# Revit family: plfy-p22_71gmg7_60Hz
name_source: partatom
category: 機械設備
units: mm (PartAtom-declared; Revit-internal decimal feet)

## family parameters
OmniClass タイトル = Split System Air Conditioning Units
OmniClass 番号 = 23.75.10.24.21.27.27
パーツ タイプ = 標準
ロード時にボイドで切り取り = いいえ
丸型コネクタ寸法 = 直径を使用
作業面ベース = いいえ
共有 = いいえ
常に垂直 = はい
部屋計算ポイント = はい

## types (6) — shared parameters
Clearance Back = 500  [stored 1.64042 ft]
Clearance Bottom = 1000  [stored 3.28084 ft]
Clearance Front = 500  [stored 1.64042 ft]
Clearance Left = 500  [stored 1.64042 ft]
Clearance Right = 500  [stored 1.64042 ft]
Clearance Top = 305  [stored 1.00066 ft]
Depth = 670  [stored 2.19816 ft]
Height = 298  [stored 0.97769 ft]
IfcExportAs = IfcUnitaryEquipmentType
IfcExportType = AIRCONDITIONINGUNIT
OmniClassCode = 23-33 17 13 11
Panel Depth = 760  [stored 2.49344 ft]
Panel Height = 15  [stored 0.0492126 ft]
Panel Width = 760  [stored 2.49344 ft]
URL = https://www.mitsubishielectric.co.jp
Uniclass2015Code = Pr_70_65_03_84
Uniclass2015Title = Split coil remote air cooled condensing units
Uniclass2015Version = Systems v1.9
Width = 670  [stored 2.19816 ft]
ケーブルサイズ = 0 mm
サービススペース = はい
ドレン管径 = 25 mm
ドレン管径 (外径) = 32 mm
ドレン管高さ = 227  [stored 0.744751 ft]
パネルマテリアル = <カテゴリ別>
仕様書バージョン = Version1.0
企業コード = 108420
冷媒ガス管高さ = 183
冷媒液管高さ = 159  [stored 0.521654 ft]
冷媒管径 = 100 mm
冷媒高低圧ガス管径 = 0 mm
分類コード = 50053003123030
加湿給水管径 = 0 mm
参照している仕様書等のバージョン = 公共建築工事標準仕様書（機械設備工事編）平成31年度版
吊りボルト_H = 134
吊り位置X = 640  [stored 2.09974 ft]
吊り位置Y = 507  [stored 1.66339 ft]
周波数 = 60 Hz
呼称 = パッケージ形空気調和機_室内機
始動方式 = 直入
形式 = カセット形（4方向吹出形）
推奨ブレーカー容量 = 0 A
本体マテリアル = <カテゴリ別>
極数 = 1
法定耐用年数 = 6
消費電力_加湿器 = 0.00 kW
消費電力_電気ヒーター = 0.00 kW
発停方法 = 付属スイッチ
相 = 1
積算_科目 = 1 空気調和設備
符号 = PAC-CK4
製品リリース年月 = 2021/5/10
製品出荷対象 = 国内
製造元 = 三菱電機株式会社
設置方法 = カセット形
設計冷房能力 = 0 kW
設計冷房能力_顕熱 = 0 kW
設計暖房能力 = 0.00 kW
説明 = ビル用マルチ 4方向天井カセット形<コンパクトタイプ>
負荷分類 = 3_ファン類
運転質量 = 0.00 kg
電動機出力_送風機 = 0.05 kW
電圧 = 200 V
電圧_電気ヒーター = 0 V
zero-valued in all types: 価格, 有効加湿量, 電源_H

## per-type parameters (varying)
- 天井4方向_PLFY-P22GMG7: MAX風量=600.0 m³/h; MID風量=570.0 m³/h; MID風量2=540.0 m³/h; MIN風量=510.0 m³/h; 冷媒ガス管径=13 mm; 冷媒ガス管長さ=76  [stored 0.249344 ft]; 冷媒液管径=6 mm; 冷媒液管長さ=71  [stored 0.23294 ft]; 冷媒管径符号=Ac; 冷房能力=2.2 kW; 暖房能力=2.50 kW; 構成品番=PLFY-P22GMG; 消費電力=0.02 kW; 消費電力_冷房=0.02 kW; 消費電力_暖房=0.02 kW; 製品質量=19.60 kg; 質量=23.52 kg; 音響パワーレベル(dB)=50; 音響パワーレベル（中1）(dB)=49; 音響パワーレベル（中2）(dB)=48; 音響パワーレベル（弱）(dB)=47; 風量=600.0 m³/h; 風量（中）（m3／min）=9.5; 風量（弱）（m3／min）=9; 風量（強）（m3／min）=10; 風量（静）（m3／min）=8.5
- 天井4方向_PLFY-P28GMG7: MAX風量=600.0 m³/h; MID風量=570.0 m³/h; MID風量2=540.0 m³/h; MIN風量=510.0 m³/h; 冷媒ガス管径=13 mm; 冷媒ガス管長さ=76  [stored 0.249344 ft]; 冷媒液管径=6 mm; 冷媒液管長さ=71  [stored 0.23294 ft]; 冷媒管径符号=Ac; 冷房能力=2.8 kW; 暖房能力=3.20 kW; 構成品番=PLFY-P28GMG; 消費電力=0.02 kW; 消費電力_冷房=0.02 kW; 消費電力_暖房=0.02 kW; 製品質量=19.60 kg; 質量=23.52 kg; 音響パワーレベル(dB)=50; 音響パワーレベル（中1）(dB)=49; 音響パワーレベル（中2）(dB)=48; 音響パワーレベル（弱）(dB)=47; 風量=600.0 m³/h; 風量（中）（m3／min）=9.5; 風量（弱）（m3／min）=9; 風量（強）（m3／min）=10; 風量（静）（m3／min）=8.5
- 天井4方向_PLFY-P36GMG7: MAX風量=720.0 m³/h; MID風量=630.0 m³/h; MID風量2=600.0 m³/h; MIN風量=570.0 m³/h; 冷媒ガス管径=13 mm; 冷媒ガス管長さ=76  [stored 0.249344 ft]; 冷媒液管径=6 mm; 冷媒液管長さ=71  [stored 0.23294 ft]; 冷媒管径符号=Ac; 冷房能力=3.6 kW; 暖房能力=4.00 kW; 構成品番=PLFY-P36GMG; 消費電力=0.03 kW; 消費電力_冷房=0.03 kW; 消費電力_暖房=0.03 kW; 製品質量=19.60 kg; 質量=23.52 kg; 音響パワーレベル(dB)=54; 音響パワーレベル（中1）(dB)=51; 音響パワーレベル（中2）(dB)=50; 音響パワーレベル（弱）(dB)=49; 風量=720.0 m³/h; 風量（中）（m3／min）=10.5; 風量（弱）（m3／min）=10; 風量（強）（m3／min）=12; 風量（静）（m3／min）=9.5
- 天井4方向_PLFY-P45GMG7: MAX風量=750.0 m³/h; MID風量=630.0 m³/h; MID風量2=600.0 m³/h; MIN風量=570.0 m³/h; 冷媒ガス管径=13 mm; 冷媒ガス管長さ=76  [stored 0.249344 ft]; 冷媒液管径=6 mm; 冷媒液管長さ=71  [stored 0.23294 ft]; 冷媒管径符号=Ac; 冷房能力=4.5 kW; 暖房能力=5.00 kW; 構成品番=PLFY-P45GMG; 消費電力=0.03 kW; 消費電力_冷房=0.03 kW; 消費電力_暖房=0.03 kW; 製品質量=19.60 kg; 質量=23.52 kg; 音響パワーレベル(dB)=54; 音響パワーレベル（中1）(dB)=52; 音響パワーレベル（中2）(dB)=50; 音響パワーレベル（弱）(dB)=49; 風量=750.0 m³/h; 風量（中）（m3／min）=10.5; 風量（弱）（m3／min）=10; 風量（強）（m3／min）=12.5; 風量（静）（m3／min）=9.5
- 天井4方向_PLFY-P56GMG7: MAX風量=780.0 m³/h; MID風量=750.0 m³/h; MID風量2=690.0 m³/h; MIN風量=600.0 m³/h; 冷媒ガス管径=13 mm; 冷媒ガス管長さ=76  [stored 0.249344 ft]; 冷媒液管径=6 mm; 冷媒液管長さ=71  [stored 0.23294 ft]; 冷媒管径符号=Ac; 冷房能力=5.6 kW; 暖房能力=6.30 kW; 構成品番=PLFY-P56GMG; 消費電力=0.03 kW; 消費電力_冷房=0.03 kW; 消費電力_暖房=0.03 kW; 製品質量=20.60 kg; 質量=24.72 kg; 音響パワーレベル(dB)=55; 音響パワーレベル（中1）(dB)=54; 音響パワーレベル（中2）(dB)=53; 音響パワーレベル（弱）(dB)=50; 風量=780.0 m³/h; 風量（中）（m3／min）=12.5; 風量（弱）（m3／min）=11.5; 風量（強）（m3／min）=13; 風量（静）（m3／min）=10
- 天井4方向_PLFY-P71GMG7: MAX風量=900.0 m³/h; MID風量=750.0 m³/h; MID風量2=690.0 m³/h; MIN風量=660.0 m³/h; 冷媒ガス管径=16 mm; 冷媒ガス管長さ=80  [stored 0.262467 ft]; 冷媒液管径=10 mm; 冷媒液管長さ=75; 冷媒管径符号=Bd; 冷房能力=7.1 kW; 暖房能力=8.00 kW; 構成品番=PLFY-P71GMG; 消費電力=0.04 kW; 消費電力_冷房=0.04 kW; 消費電力_暖房=0.04 kW; 製品質量=20.60 kg; 質量=24.72 kg; 音響パワーレベル(dB)=43; 音響パワーレベル（中1）(dB)=40; 音響パワーレベル（中2）(dB)=39; 音響パワーレベル（弱）(dB)=38; 風量=900.0 m³/h; 風量（中）（m3／min）=12.5; 風量（弱）（m3／min）=11.5; 風量（強）（m3／min）=15; 風量（静）（m3／min）=11

note: [stored X ft] marks values corroborated as IEEE doubles in the binary element streams (Revit-internal decimal feet)

## geometry (parser evidence)
native form markers: Blend x4
no freeform markers — native parametric forms only
